# Revit family: VRV1-AF
name_source: partatom
category: Арматура воздуховодов
units: mm (PartAtom-declared; Revit-internal decimal feet)

## family parameters
Всегда вертикально = Да
На основе рабочей плоскости = Нет
Общий = Нет
При загрузке вырезать с полостями = Нет
Размер круглого соединителя = Использовать диаметр
Тип детали = Присоединяется

## types (11) — shared parameters
00_20_Manufacturer = BLAUBERG
00_20_Name = Backdraft damper
A = 1135 мм
Casing Material = Metal, painted, grey, matt RAL 7040
E1 = 830 мм
Load Classification = HVAC
Maintenance zone material = <По категории>
Изготовитель = BLAUBERG
zero-valued in all types: Отметка по умолчанию

## per-type parameters (varying)
| type | D1 | D2 | Diameter | Dn | Dy | L | Length | R1 | Weight | d | l | n | t |
| VRV1-AF-400 | 450 мм | 490 мм | 490 мм | 410 мм | 400 мм | 500 мм | 500 мм | 225 мм | 8.10 кг | 8 мм | 250 мм | 12 | 495 мм |
| VRV1-AF-450 | 500 мм | 540 мм | 540 мм | 460 мм | 450 мм | 550 мм | 550 мм | 250 мм | 9.80 кг | 8 мм | 275 мм | 12 | 545 мм |
| VRV1-AF-500 | 560 мм | 600 мм | 600 мм | 510 мм | 500 мм | 600 мм | 600 мм | 280 мм | 14.40 кг | 12 мм | 300 мм | 12 | 595 мм |
| VRV1-AF-560 | 620 мм | 660 мм | 660 мм | 570 мм | 560 мм | 660 мм | 660 мм | 310 мм | 17.50 кг | 12 мм | 330 мм | 12 | 655 мм |
| VRV1-AF-630 | 690 мм | 730 мм | 730 мм | 640 мм | 630 мм | 730 мм | 730 мм | 345 мм | 21.40 кг | 12 мм | 365 мм | 12 | 725 мм |
| VRV1-AF-710 | 770 мм | 810 мм | 810 мм | 720 мм | 710 мм | 810 мм | 810 мм | 385 мм | 26.80 кг | 12 мм | 405 мм | 16 | 805 мм |
| VRV1-AF-800 | 860 мм | 900 мм | 900 мм | 810 мм | 800 мм | 900 мм | 900 мм | 430 мм | 33.20 кг | 12 мм | 450 мм | 16 | 895 мм |
| VRV1-AF-900 | 970 мм | 1015 мм | 1015 мм | 910 мм | 900 мм | 1000 мм | 1000 мм | 485 мм | 53.70 кг | 15 мм | 500 мм | 16 | 995 мм |
| VRV1-AF-1000 | 1070 мм | 1115 мм | 1115 мм | 1010 мм | 1000 мм | 1100 мм | 1100 мм | 535 мм | 65.00 кг | 15 мм | 550 мм | 16 | 1095 мм |
| VRV1-AF-1120 | 1190 мм | 1270 мм | 1270 мм | 1130 мм | 1120 мм | 1220 мм | 1220 мм | 595 мм | 82.10 кг | 15 мм | 610 мм | 20 | 1215 мм |
| VRV1-AF-1250 | 1320 мм | 1400 мм | 1400 мм | 1260 мм | 1250 мм | 1350 мм | 1350 мм | 660 мм | 100.30 кг | 15 мм | 675 мм | 20 | 1345 мм |

note: column(s) folded — value = type name in every type: 00_20_Type
